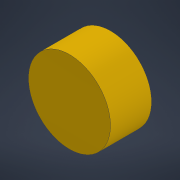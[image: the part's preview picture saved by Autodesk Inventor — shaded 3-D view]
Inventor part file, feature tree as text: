
AUTODESK INVENTOR PART (.ipt)
format: ipt  version: 2021 (Build 250183000, 183)  size: 89,088 bytes
history: native  units: mm
features: extrude x1, sketch x1
ambient origin geometry x8: Origin, YZ Plane, XZ Plane, XY Plane, X Axis, Y Axis, Z Axis, Center Point
bodies: Solid1 (feature_tree)
feature tree (2):
  extrude  "Extrusion1"  Depth=10.0mm
  sketch  "Sketch1"  dims[d0=10.0mm d1=0.0mm d2=20.0mm]
